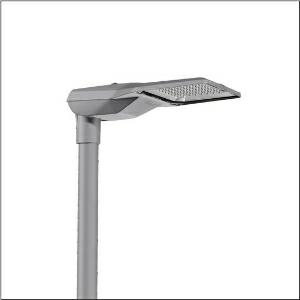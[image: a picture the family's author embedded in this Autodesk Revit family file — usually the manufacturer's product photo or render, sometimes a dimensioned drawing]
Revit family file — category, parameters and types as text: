
# Revit family: streetlight_sl_21_iq_midi___st1_0a_5xe3d31v08mb_ff90
name_source: partatom
category: Lighting Fixtures
units: mm (PartAtom-declared; Revit-internal decimal feet)

## family parameters
Cut with Voids When Loaded = No
Host = Face
Light Source = No
Part Type = Normal
Room Calculation Point = No
Round Connector Dimension = Use Diameter
Shared = No

## types (1)
- --- (1 x LED, 18340 lm, 129.3 W, 3000K)
    Apparent Load = 129 VA
    CIE Flux Codes = 37 72 97 100 100
    Color Rendering = 70
    Color Temperature = 3000K
    Default Elevation = 1800 mm
    Description = Streetlight SL 21 iQ midi, mast luminaire, primary light control with lens, of PMMA, primary optical cover: cover, of toughened safety glass, transparent, light distribution: ST1.0a, light emission: direct distribution, primary light characteristic: asymmetric, installation type: post-top, side-entry, LED, High Power LED, rated luminous flux: 18.340lm, luminous efficacy: 142lm/W, light colour: 730, colour temperature: 3000K, control gear: iQ-Street Remote, D4i with power reduction, control: pre-setting: logarithmic dimming characteristic, Street-Remote, Auto-Match, Temp-Guard, Lumen-Switch, Night-Set, Smart-Wire, Light-Fading, Desk-Remote (wireless, voltage-free reading and setting of iQ features in the workshop via application-optimized NFC function/RFID function), optimised constant luminous flux control (CLO 2.0), mains connection: 230..240V, AC, 50/60Hz, start of lifetime: 129W, end of service life: 142W, reduction: 56W, luminaire housing, of diecast aluminium, powder-coated, SITECO metallic grey (DB 702S), corrosivity category C5 high according to DIN EN ISO 12944, please order mast flange separately, inclination adjustable: 0°, 5°, 10°, 15°, sealing non-destructively replaceable, multi-level sealing system, length: 644mm, width: 335mm, height: 110mm, mast flange for spigot size: 42mm (side-entry): 5XC10008XM4, 60/48mm (side-entry/post-top): 5XC10108XM2, 76/60mm (side-entry/post-top): 5XC10108XM1, mounting height: 4..8m, Smart Interface above, protection rating (complete): IP66, insulation class (complete): insulation class II (safety insulation), certification: CE, ENEC, ENEC+, VDE, impact resistance: IK10, permissible operating ambient temperature for outdoor applications: -40..+50°C, standard-compliant lighting for roads and squares, packaging unit: 1 piece

Light Distribution: ST1.0a
    Height = 111 mm
    Lamp = 1 x LED
    Lamp Light Flux = 18340 lm
    Lamp Power = 129.3 W
    Lamp count = 1
    Length = 644 mm
    Luminous efficacy = 142 lm/W
    Manufacturer = Siteco
    ModVariant = No
    Model = 5XE3D31V08MB
    Number of Poles = 1
    OnlyDefault = Yes
    Power Factor = 1
    Product Name = Streetlight SL 21 iQ midi | ST1.0a
    Product group = mast luminaire | pylon top
    ProductGroupID = 6100
    Protection Class = Protection class II
    Protection Degree = IP 66
    RLX_Detail_Level = 1
    RLX_Emergency_Light_Flux = 0 lm
    RLX_Emergency_Type = 0
    RLX_Emergency_Type_DB = No
    RlxData = <blob elided: 91301 chars, md5=69a95bf3>
    Socket = socket
    Standby Power = 0 W
    System Light Flux = 18340 lm
    System Power = 129 W
    Type Comments = factory setting: luminous flux: 100 % | dim-lin: 254 | 672 mA
    Type Image = l_1004302.jpg
    URL = http://relux.com
    VarID = @adj_114767
    Voltage = 0 V
    Weight = 0.00 kg
    Width = 336 mm

## geometry (parser evidence)
native form markers: Blend x4, Sweep x12
no freeform markers — native parametric forms only
